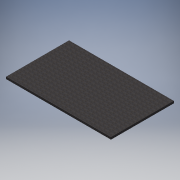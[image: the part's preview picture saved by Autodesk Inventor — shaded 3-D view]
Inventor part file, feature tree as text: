
AUTODESK INVENTOR PART (.ipt)
format: ipt  version: 2017 (Build 210142000, 142)  size: 101,376 bytes
history: native  units: mm
features: extrude x1, sketch x1
ambient origin geometry x8: Origin, YZ Plane, XZ Plane, XY Plane, X Axis, Y Axis, Z Axis, Center Point
bodies: Volumenkörper1 (feature_tree)
feature tree (2):
  extrude  "Extrusion1"  Depth=5000.0mm
  sketch  "Skizze1"  dims[d0=3000.0mm d1=5000.0mm d2=100.0mm d3=0.0mm]
